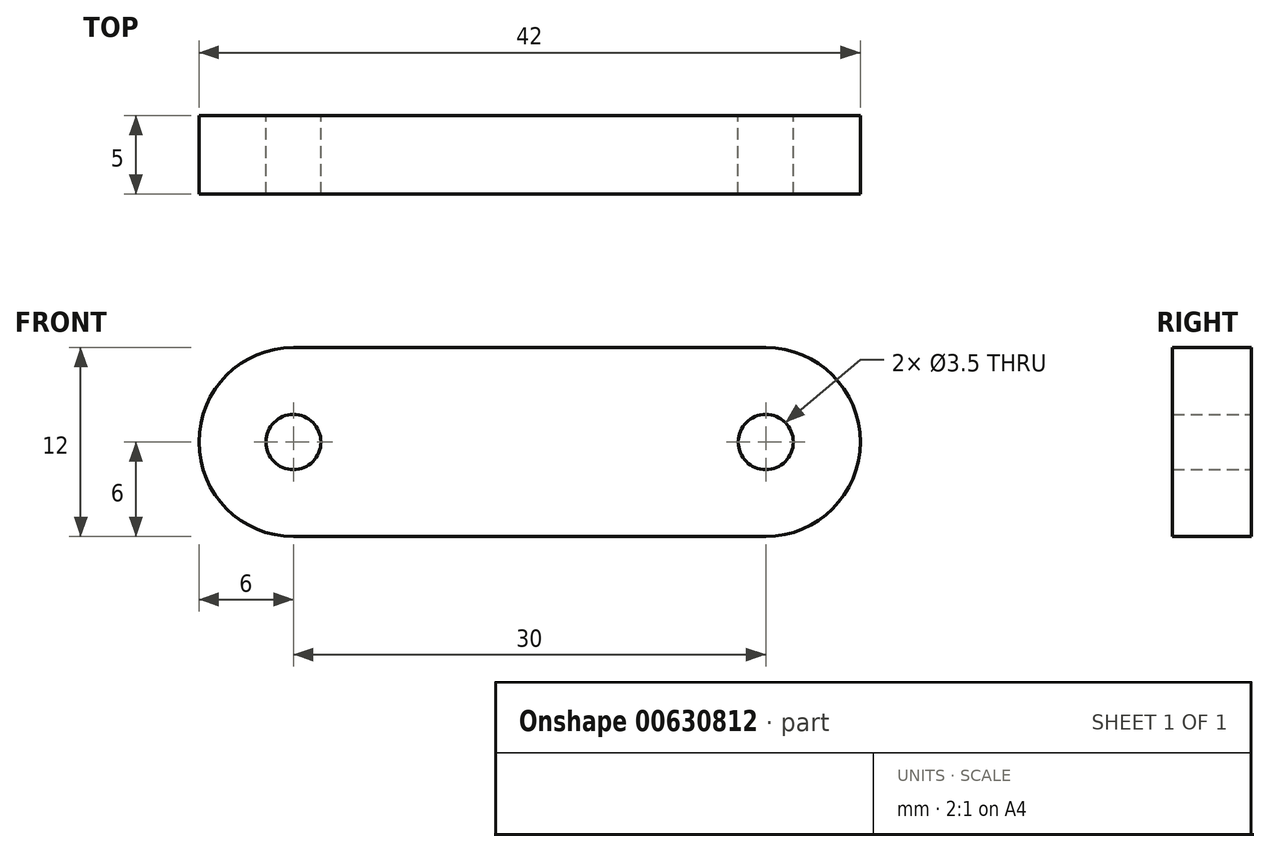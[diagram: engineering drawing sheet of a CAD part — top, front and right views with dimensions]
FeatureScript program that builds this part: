
annotation { "Feature Type Name" : "Feature", "Feature Type Description" : "" }
export const myFeature = defineFeature(function(context is Context, id is Id, definition is map)
    precondition{}
    {
        {
            var Q0;
            Q0=qCreatedBy(makeId("Front.planeOp"),FACE);
            var sketch = newSketch(context, id + "F0", { "sketchPlane" : qUnion([Q0])});
            skCircle(sketch, "E0", {"center": v(15, 0) * mm, "radius": 1.75 * mm});
            skCircle(sketch, "E1", {"center": v(-15, 0) * mm, "radius": 1.75 * mm});
            skLineSegment(sketch, "E2", {"start": v(-15, 0) * mm, "end": v(15, 0) * mm});
            skArc(sketch, "E3.0.startCap", {"start": v(-15, -6) * mm, "mid": v(-21, 0) * mm, "end": v(-15, 6) * mm});
            skArc(sketch, "E3.0.endCap", {"start": v(15, 6) * mm, "mid": v(21, 0) * mm, "end": v(15, -6) * mm});
            skLineSegment(sketch, "E3.0.left", {"start": v(-15, 6) * mm, "end": v(15, 6) * mm});
            skLineSegment(sketch, "E3.0.right", {"start": v(-15, -6) * mm, "end": v(15, -6) * mm});
            skSolve(sketch);
        }
        {
            var Q0;
            Q0=qSketchRegion(id+"F0",true);
            extrude(context, id + "F1", {"entities" : qUnion([Q0]), "depth" : 5 * mm, "offsetDistance" : 25 * mm});
        }
    });
